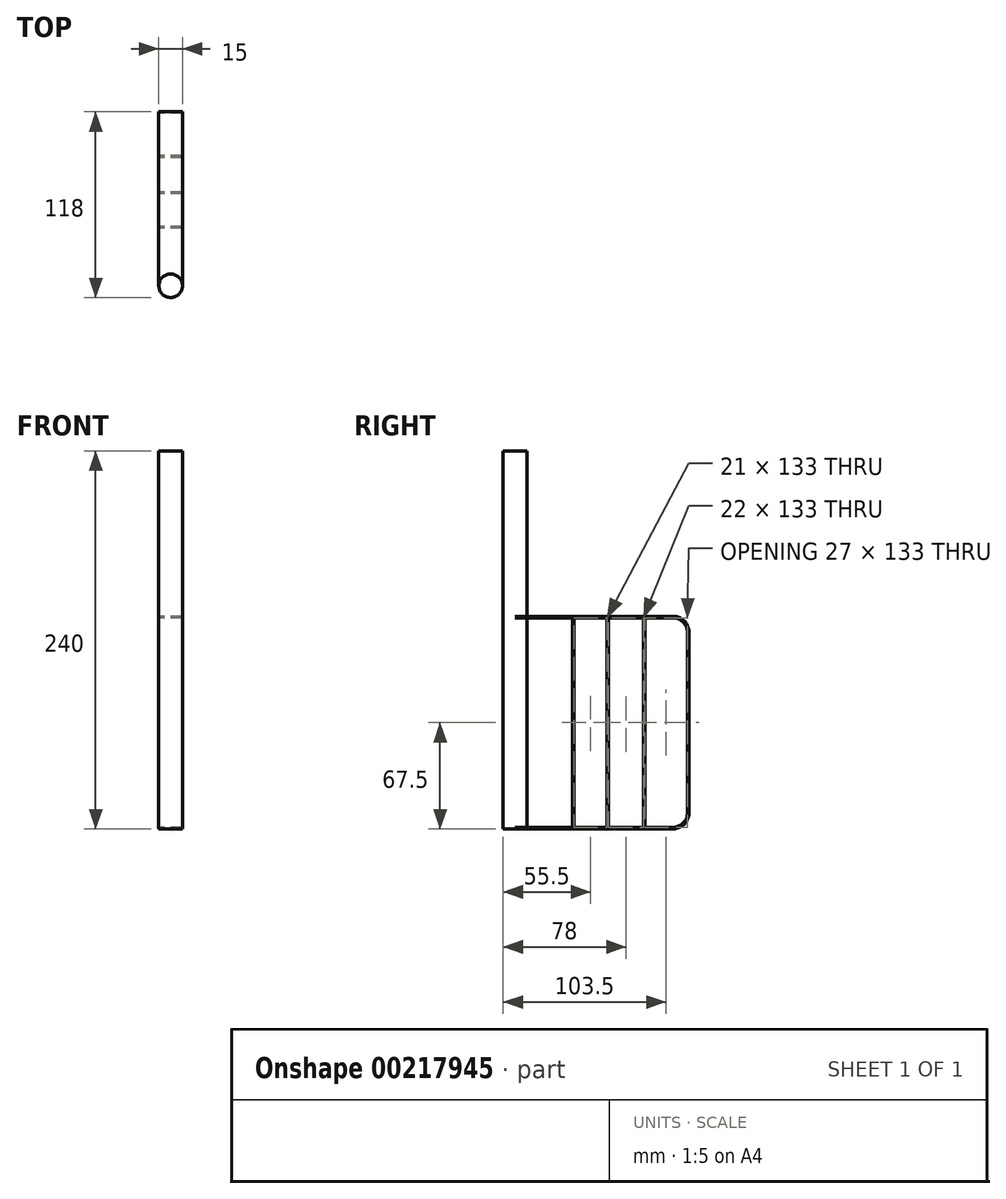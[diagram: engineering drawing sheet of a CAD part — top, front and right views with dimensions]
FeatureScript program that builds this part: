
annotation { "Feature Type Name" : "Feature", "Feature Type Description" : "" }
export const myFeature = defineFeature(function(context is Context, id is Id, definition is map)
    precondition{}
    {
        {
            var Q0;
            Q0=qCreatedBy(makeId("Top.planeOp"),FACE);
            var sketch = newSketch(context, id + "F0", { "sketchPlane" : qUnion([Q0])});
            skCircle(sketch, "E0", {"center": v(0, 0) * mm, "radius": 7.5 * mm});
            skSolve(sketch);
        }
        {
            var Q0;
            Q0=makeQuery(id+"F0.imprint","IMPRINT",FACE,{"disambiguationData":[TD([[makeQuery(id+"F0.imprint","IMPRINT",EDGE,{"derivedFrom":sQuery(id+"F0.wireOp",EDGE,"E0")}),1.0]])]});
            extrude(context, id + "F1", {"entities" : qUnion([Q0]), "depth" : 240 * mm});
        }
        {
            var Q0;
            Q0=qCreatedBy(makeId("Right.planeOp"),FACE);
            var sketch = newSketch(context, id + "F2", { "sketchPlane" : qUnion([Q0])});
            skLineSegment(sketch, "E1.bottom", {"start": v(0, 0) * mm, "end": v(100.5, 0) * mm});
            skLineSegment(sketch, "E1.top", {"start": v(0, 135) * mm, "end": v(100.5, 135) * mm});
            skLineSegment(sketch, "E1.left", {"start": v(0, 0) * mm, "end": v(0, 135) * mm, "construction": true});
            skLineSegment(sketch, "E1.right", {"start": v(110.5, 10) * mm, "end": v(110.5, 125) * mm});
            skLineSegment(sketch, "E2.0", {"start": v(-7.5, 0) * mm, "end": v(7.5, 0) * mm, "construction": true});
            skPoint(sketch, "E3.visualSharp", {"position": v(110.5, 135) * mm});
            skArc(sketch, "E3.filletArc", {"start": v(110.5, 125) * mm, "mid": v(107.57, 132.07) * mm, "end": v(100.5, 135) * mm});
            skPoint(sketch, "E4.visualSharp", {"position": v(110.5, 0) * mm});
            skArc(sketch, "E4.filletArc", {"start": v(100.5, 0) * mm, "mid": v(107.57, 2.93) * mm, "end": v(110.5, 10) * mm});
            skLineSegment(sketch, "E5.0", {"start": v(0, 1) * mm, "end": v(36.5, 1) * mm});
            skLineSegment(sketch, "E5.1", {"start": v(0, 134) * mm, "end": v(36.5, 134) * mm});
            skArc(sketch, "E5.2", {"start": v(109.5, 125) * mm, "mid": v(106.86, 131.36) * mm, "end": v(100.5, 134) * mm});
            skLineSegment(sketch, "E5.3", {"start": v(109.5, 10) * mm, "end": v(109.5, 125) * mm});
            skArc(sketch, "E5.4", {"start": v(100.5, 1) * mm, "mid": v(106.86, 3.64) * mm, "end": v(109.5, 10) * mm});
            skLineSegment(sketch, "E6.left", {"start": v(36.5, 134) * mm, "end": v(36.5, 1) * mm});
            skLineSegment(sketch, "E6.right", {"start": v(37.5, 134) * mm, "end": v(37.5, 1) * mm});
            skLineSegment(sketch, "E7.left", {"start": v(58.5, 134) * mm, "end": v(58.5, 1) * mm});
            skLineSegment(sketch, "E7.right", {"start": v(59.5, 134) * mm, "end": v(59.5, 1) * mm});
            skLineSegment(sketch, "E8.left", {"start": v(82.5, 134) * mm, "end": v(82.5, 1) * mm});
            skLineSegment(sketch, "E8.right", {"start": v(81.5, 134) * mm, "end": v(81.5, 1) * mm});
            skLineSegment(sketch, "E9.trimOffspring", {"start": v(59.5, 1) * mm, "end": v(81.5, 1) * mm});
            skLineSegment(sketch, "E10.trimOffspring", {"start": v(82.5, 1) * mm, "end": v(100.5, 1) * mm});
            skLineSegment(sketch, "E11.trimOffspring", {"start": v(37.5, 1) * mm, "end": v(58.5, 1) * mm});
            skLineSegment(sketch, "E12.trimOffspring", {"start": v(37.5, 134) * mm, "end": v(58.5, 134) * mm});
            skLineSegment(sketch, "E13.trimOffspring", {"start": v(59.5, 134) * mm, "end": v(81.5, 134) * mm});
            skLineSegment(sketch, "E14.trimOffspring", {"start": v(82.5, 134) * mm, "end": v(100.5, 134) * mm});
            skLineSegment(sketch, "E15", {"start": v(0, 135) * mm, "end": v(0, 134) * mm});
            skLineSegment(sketch, "E16", {"start": v(0, 1) * mm, "end": v(0, 0) * mm});
            skSolve(sketch);
        }
        {
            var Q0;
            Q0=makeQuery(id+"F2.imprint","IMPRINT",FACE,{"disambiguationData":[TD([[makeQuery(id+"F2.imprint","IMPRINT",EDGE,{"derivedFrom":sQuery(id+"F2.wireOp",EDGE,"E1.bottom")}),1.0]])]});
            extrude(context, id + "F3", {"entities" : qUnion([Q0]), "operationType" : NewBodyOperationType.ADD, "endBound" : BoundingType.SYMMETRIC, "depth" : 15 * mm});
        }
    });
